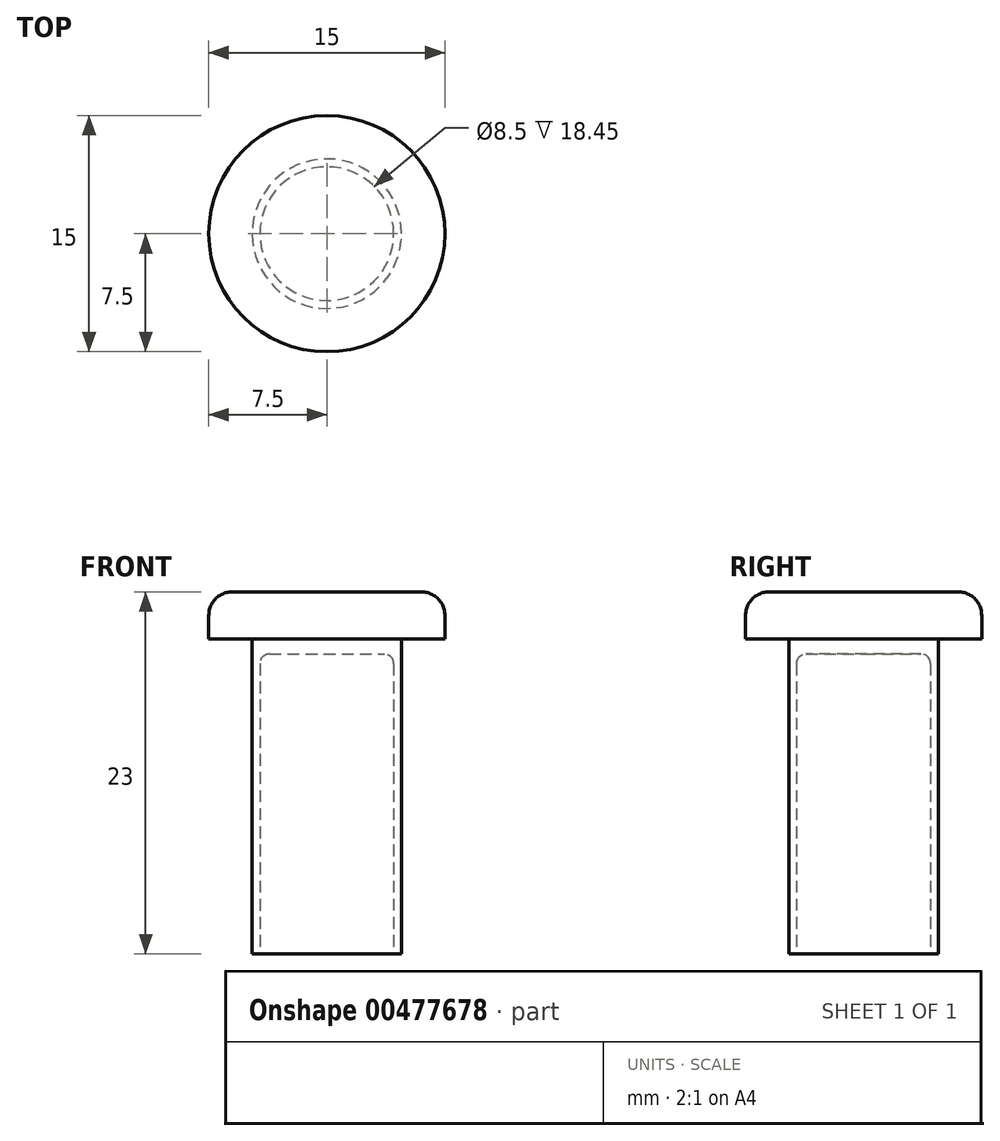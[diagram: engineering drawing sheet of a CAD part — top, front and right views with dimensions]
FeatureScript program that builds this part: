
annotation { "Feature Type Name" : "Feature", "Feature Type Description" : "" }
export const myFeature = defineFeature(function(context is Context, id is Id, definition is map)
    precondition{}
    {
        {
            var Q0;
            Q0=qCreatedBy(makeId("Front.planeOp"),FACE);
            var sketch = newSketch(context, id + "F0", { "sketchPlane" : qUnion([Q0])});
            skLineSegment(sketch, "E0", {"start": v(0, 0) * mm, "end": v(0, 7.09) * mm, "construction": true});
            skLineSegment(sketch, "E1", {"start": v(-4.25, 0) * mm, "end": v(-4.75, 0) * mm});
            skLineSegment(sketch, "E2", {"start": v(-4.75, 0) * mm, "end": v(-4.75, 11.8) * mm});
            skLineSegment(sketch, "E3", {"start": v(-4.75, 20) * mm, "end": v(-7.5, 20) * mm});
            skLineSegment(sketch, "E4", {"start": v(-7.5, 20) * mm, "end": v(-7.5, 21.5) * mm});
            skLineSegment(sketch, "E5.MirrorCS", {"start": v(4.75, 0) * mm, "end": v(4.75, 20) * mm, "construction": true});
            skLineSegment(sketch, "E6.MirrorCS", {"start": v(4.75, 20) * mm, "end": v(7.5, 20) * mm, "construction": true});
            skLineSegment(sketch, "E7.MirrorCS", {"start": v(7.5, 20) * mm, "end": v(7.5, 21.5) * mm, "construction": true});
            skLineSegment(sketch, "E8.MirrorCS", {"start": v(4.25, 19.05) * mm, "end": v(4.25, 0) * mm, "construction": true});
            skLineSegment(sketch, "E9.MirrorCS", {"start": v(4.25, 0) * mm, "end": v(4.75, 0) * mm, "construction": true});
            skPoint(sketch, "E10.MirrorCS.end.orphan", {"position": v(4.25, 19.05) * mm});
            skPoint(sketch, "E10.MirrorCS.start.orphan", {"position": v(7.5, 21.5) * mm});
            skLineSegment(sketch, "E11", {"start": v(-7.5, 21.5) * mm, "end": v(-7.5, 21.5) * mm});
            skLineSegment(sketch, "E12", {"start": v(0, 23) * mm, "end": v(0, 19.05) * mm});
            skLineSegment(sketch, "E13", {"start": v(0, 19.05) * mm, "end": v(-3.65, 19.05) * mm});
            skArc(sketch, "E14", {"start": v(-7.5, 21.5) * mm, "mid": v(-7.06, 22.56) * mm, "end": v(-6, 23) * mm});
            skLineSegment(sketch, "E15", {"start": v(-6, 23) * mm, "end": v(0, 23) * mm});
            skLineSegment(sketch, "E16", {"start": v(-6, 21.5) * mm, "end": v(-6, 23) * mm, "construction": true});
            skArc(sketch, "E17", {"start": v(-4.25, 18.45) * mm, "mid": v(-4.07, 18.87) * mm, "end": v(-3.65, 19.05) * mm});
            skLineSegment(sketch, "E18", {"start": v(-4.25, 18.45) * mm, "end": v(-4.25, 0) * mm});
            skPoint(sketch, "E19.start.orphan", {"position": v(-4.25, 19.05) * mm});
            skLineSegment(sketch, "E20", {"start": v(-4.75, 11.8) * mm, "end": v(-4.75, 20) * mm});
            skSolve(sketch);
        }
        {
            var Q0;
            Q0 = qSketchRegion(id + "F0", true);
            var Q1;
            Q1=sQuery(id+"F0.wireOp",EDGE,"E0");
            revolve(context, id + "F1", {"entities" : qUnion([Q0]), "axis" : qUnion([Q1]), "revolveType" : RevolveType.FULL});
        }
    });
